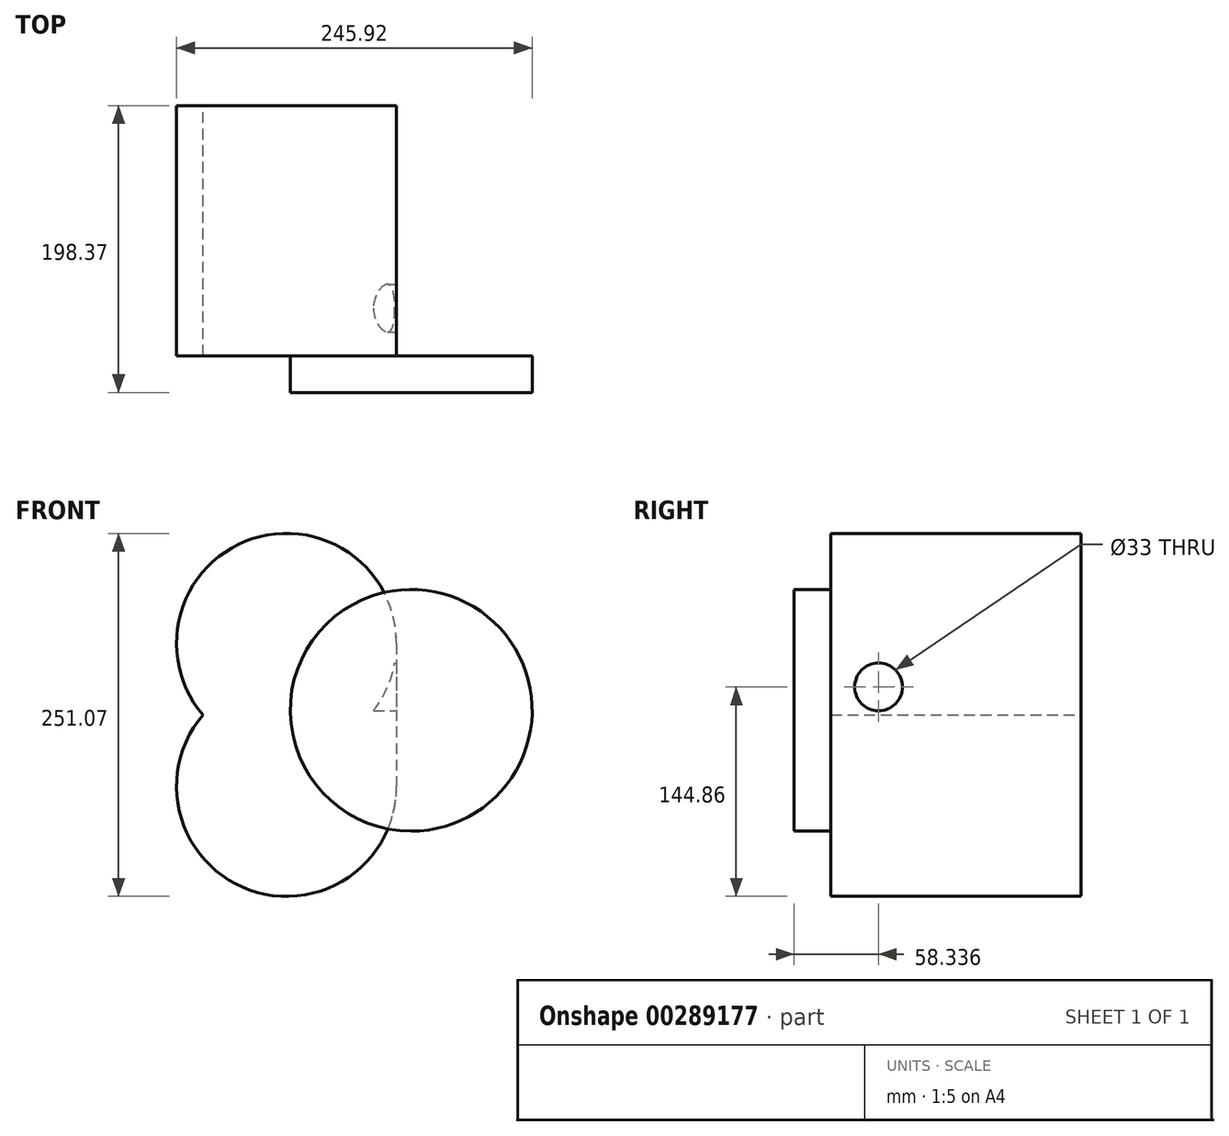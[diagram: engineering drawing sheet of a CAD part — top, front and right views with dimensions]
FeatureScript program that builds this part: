
annotation { "Feature Type Name" : "Feature", "Feature Type Description" : "" }
export const myFeature = defineFeature(function(context is Context, id is Id, definition is map)
    precondition{}
    {
        {
            var Q0;
            Q0=qCreatedBy(makeId("Front.planeOp"),FACE);
            var sketch = newSketch(context, id + "F0", { "sketchPlane" : qUnion([Q0])});
            skLineSegment(sketch, "E0.bottom", {"start": v(-178.94, -7.47) * mm, "end": v(-102.88, -7.47) * mm});
            skLineSegment(sketch, "E0.top", {"start": v(-178.94, -106.42) * mm, "end": v(-102.88, -106.42) * mm});
            skLineSegment(sketch, "E0.left", {"start": v(-178.94, -7.47) * mm, "end": v(-178.94, -106.42) * mm});
            skLineSegment(sketch, "E0.right", {"start": v(-102.88, -7.47) * mm, "end": v(-102.88, -106.42) * mm});
            skSolve(sketch);
        }
        {
            var Q0;
            Q0=makeQuery(id+"F0.imprint","IMPRINT",FACE,{"disambiguationData":[TD([[makeQuery(id+"F0.imprint","IMPRINT",EDGE,{"derivedFrom":sQuery(id+"F0.wireOp",EDGE,"E0.bottom")}),-1.0]])]});
            extrude(context, id + "F1", {"entities" : qUnion([Q0]), "oppositeDirection" : true, "depth" : 172.97 * mm});
        }
        {
            var Q0;
            Q0=qCreatedBy(makeId("Right.planeOp"),FACE);
            var sketch = newSketch(context, id + "F2", { "sketchPlane" : qUnion([Q0])});
            skCircle(sketch, "E1", {"center": v(32.94, -37.62) * mm, "radius": 16.5 * mm});
            skSolve(sketch);
        }
        {
            var Q0;
            Q0 = qSketchRegion(id + "F2", true);
            extrude(context, id + "F3", {"entities" : qUnion([Q0]), "operationType" : NewBodyOperationType.REMOVE, "oppositeDirection" : true, "depth" : 207.52 * mm});
        }
        {
            var Q0;
            Q0=makeQuery(id+"F1.opExtrude","SWEPT_FACE",FACE,{"disambiguationData":[OSD([sQuery(id+"F0.wireOp",EDGE,"E0.top")])]});
            var Q1;
            Q1=makeQuery(id+"F1.opExtrude","SWEPT_EDGE",EDGE,{"disambiguationData":[OSD([sQuery(id+"F0.wireOp",EDGE,"E0.top"),sQuery(id+"F0.wireOp",EDGE,"E0.left")])]});
            revolve(context, id + "F4", {"operationType" : NewBodyOperationType.ADD, "entities" : qUnion([Q0]), "axis" : qUnion([Q1]), "revolveType" : RevolveType.FULL});
        }
        {
            var Q0;
            Q0=makeQuery(id+"F1.opExtrude","SWEPT_FACE",FACE,{"disambiguationData":[OSD([sQuery(id+"F0.wireOp",EDGE,"E0.bottom")])]});
            var Q1;
            Q1=makeQuery(id+"F1.opExtrude","SWEPT_EDGE",EDGE,{"disambiguationData":[OSD([sQuery(id+"F0.wireOp",EDGE,"E0.bottom"),sQuery(id+"F0.wireOp",EDGE,"E0.left")])]});
            revolve(context, id + "F5", {"operationType" : NewBodyOperationType.ADD, "entities" : qUnion([Q0]), "axis" : qUnion([Q1]), "revolveType" : RevolveType.FULL});
        }
        {
            var Q0;
            Q0=qCreatedBy(makeId("Front.planeOp"),FACE);
            var sketch = newSketch(context, id + "F6", { "sketchPlane" : qUnion([Q0])});
            skCircle(sketch, "E2", {"center": v(-92.72, -53.77) * mm, "radius": 83.63 * mm});
            skSolve(sketch);
        }
        {
            var Q0;
            Q0=makeQuery(id+"F6.imprint","IMPRINT",FACE,{"disambiguationData":[TD([[makeQuery(id+"F6.imprint","IMPRINT",EDGE,{"derivedFrom":sQuery(id+"F6.wireOp",EDGE,"E2")}),1.0]])]});
            extrude(context, id + "F7", {"entities" : qUnion([Q0]), "operationType" : NewBodyOperationType.ADD, "depth" : 25.4 * mm});
        }
    });
